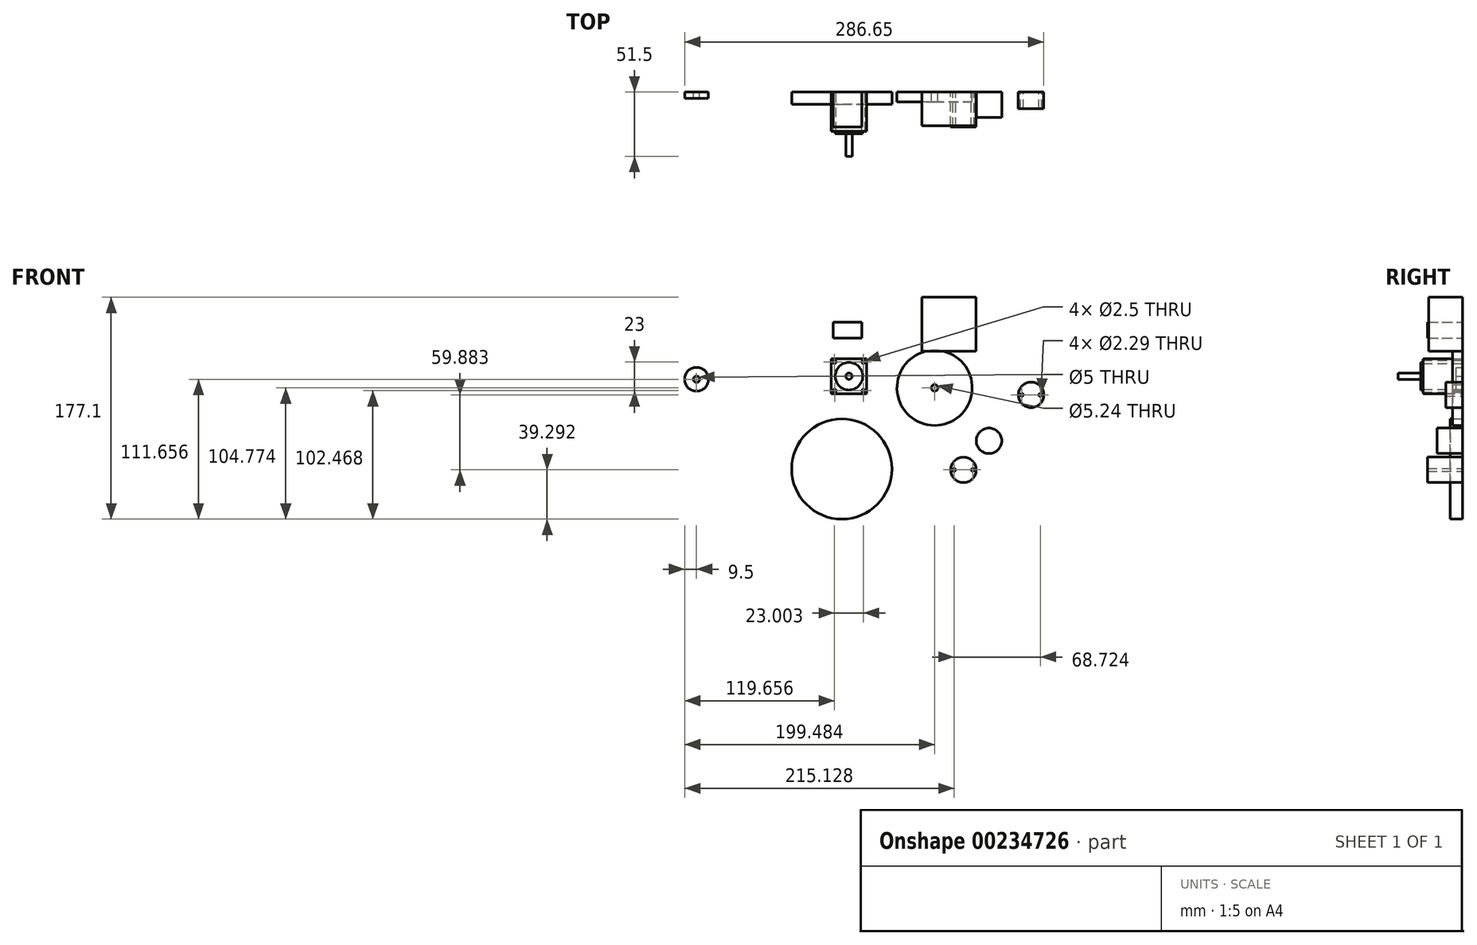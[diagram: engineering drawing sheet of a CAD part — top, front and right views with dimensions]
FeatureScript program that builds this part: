
annotation { "Feature Type Name" : "Feature", "Feature Type Description" : "" }
export const myFeature = defineFeature(function(context is Context, id is Id, definition is map)
    precondition{}
    {
        {
            var Q0;
            Q0=qCreatedBy(makeId("Front.planeOp"),FACE);
            var sketch = newSketch(context, id + "F0", { "sketchPlane" : qUnion([Q0])});
            skLineSegment(sketch, "E0.bottom", {"start": v(-36.47, 8.93) * mm, "end": v(-64.67, 8.93) * mm});
            skLineSegment(sketch, "E0.top", {"start": v(-36.47, 37.13) * mm, "end": v(-64.67, 37.13) * mm});
            skLineSegment(sketch, "E0.left", {"start": v(-36.47, 8.93) * mm, "end": v(-36.47, 37.13) * mm});
            skLineSegment(sketch, "E0.right", {"start": v(-64.67, 8.93) * mm, "end": v(-64.67, 37.13) * mm});
            skPoint(sketch, "E0.middle", {"position": v(-50.57, 23.03) * mm});
            skCircle(sketch, "E1", {"center": v(-50.57, 23.03) * mm, "radius": 2.5 * mm});
            skLineSegment(sketch, "E2", {"start": v(-62.07, 34.43) * mm, "end": v(-39.07, 34.43) * mm});
            skLineSegment(sketch, "E3", {"start": v(-62.07, 11.43) * mm, "end": v(-39.07, 11.43) * mm});
            skCircle(sketch, "E4", {"center": v(-62.07, 34.43) * mm, "radius": 1.25 * mm});
            skCircle(sketch, "E5", {"center": v(-62.07, 11.43) * mm, "radius": 1.25 * mm});
            skCircle(sketch, "E6", {"center": v(-39.07, 11.43) * mm, "radius": 1.25 * mm});
            skCircle(sketch, "E7", {"center": v(-39.07, 34.43) * mm, "radius": 1.25 * mm});
            skCircle(sketch, "E8", {"center": v(-50.57, 23.03) * mm, "radius": 11 * mm});
            skSolve(sketch);
        }
        {
            var Q0;
            Q0=makeQuery(id+"F0.imprint","IMPRINT",FACE,{"disambiguationData":[TD([[makeQuery(id+"F0.imprint","IMPRINT",EDGE,{"derivedFrom":sQuery(id+"F0.wireOp",EDGE,"E1")}),1.0]])]});
            extrude(context, id + "F1", {"entities" : qUnion([Q0]), "depth" : 51.5 * mm});
        }
        {
            var Q0;
            Q0=makeQuery(id+"F0.imprint","IMPRINT",FACE,{"disambiguationData":[TD([[makeQuery(id+"F0.imprint","IMPRINT",EDGE,{"derivedFrom":sQuery(id+"F0.wireOp",EDGE,"E1")}),-1.0]])]});
            extrude(context, id + "F2", {"entities" : qUnion([Q0]), "operationType" : NewBodyOperationType.ADD, "depth" : 33.5 * mm});
        }
        {
            var Q0;
            Q0 = qSketchRegion(id + "F0", true);
            extrude(context, id + "F3", {"entities" : qUnion([Q0]), "operationType" : NewBodyOperationType.ADD, "depth" : 31.5 * mm});
        }
        {
            var Q0;
            Q0=qCreatedBy(makeId("Front.planeOp"),FACE);
            var sketch = newSketch(context, id + "F4", { "sketchPlane" : qUnion([Q0])});
            skCircle(sketch, "E9", {"center": v(17.75, 13.73) * mm, "radius": 30 * mm});
            skCircle(sketch, "E10", {"center": v(17.75, 13.73) * mm, "radius": 2.62 * mm});
            skSolve(sketch);
        }
        {
            var Q0;
            Q0=makeQuery(id+"F4.imprint","IMPRINT",FACE,{"disambiguationData":[TD([[makeQuery(id+"F4.imprint","IMPRINT",EDGE,{"derivedFrom":sQuery(id+"F4.wireOp",EDGE,"E9")}),1.0]])]});
            extrude(context, id + "F5", {"entities" : qUnion([Q0]), "depth" : 8 * mm});
        }
        {
            var Q0;
            Q0=qCreatedBy(makeId("Front.planeOp"),FACE);
            var sketch = newSketch(context, id + "F6", { "sketchPlane" : qUnion([Q0])});
            skCircle(sketch, "E11", {"center": v(-56.28, -51.04) * mm, "radius": 40 * mm});
            skCircle(sketch, "E12", {"center": v(-172.23, 20.62) * mm, "radius": 9.5 * mm});
            skCircle(sketch, "E13", {"center": v(-172.23, 20.62) * mm, "radius": 2.5 * mm});
            skSolve(sketch);
        }
        {
            var Q0;
            Q0=makeQuery(id+"F6.imprint","IMPRINT",FACE,{"disambiguationData":[TD([[makeQuery(id+"F6.imprint","IMPRINT",EDGE,{"derivedFrom":sQuery(id+"F6.wireOp",EDGE,"E11")}),1.0]])]});
            extrude(context, id + "F7", {"entities" : qUnion([Q0]), "depth" : 10 * mm});
        }
        {
            var Q0;
            Q0=qCreatedBy(makeId("Front.planeOp"),FACE);
            var sketch = newSketch(context, id + "F8", { "sketchPlane" : qUnion([Q0])});
            skCircle(sketch, "E14", {"center": v(40.76, -51.75) * mm, "radius": 10.16 * mm});
            skCircle(sketch, "E15", {"center": v(61.22, -28.51) * mm, "radius": 10.16 * mm});
            skLineSegment(sketch, "E16", {"start": v(51.06, -28.51) * mm, "end": v(71.38, -28.51) * mm});
            skCircle(sketch, "E17", {"center": v(33.4, -51.75) * mm, "radius": 1.14 * mm});
            skCircle(sketch, "E18", {"center": v(48.13, -51.75) * mm, "radius": 1.14 * mm});
            skLineSegment(sketch, "E19", {"start": v(33.4, -51.75) * mm, "end": v(30.6, -51.75) * mm});
            skLineSegment(sketch, "E20", {"start": v(48.13, -51.75) * mm, "end": v(50.92, -51.75) * mm});
            skCircle(sketch, "E21", {"center": v(94.76, 8.14) * mm, "radius": 10.16 * mm});
            skLineSegment(sketch, "E22", {"start": v(94.76, 8.14) * mm, "end": v(102.12, 8.14) * mm});
            skLineSegment(sketch, "E23", {"start": v(94.76, 8.14) * mm, "end": v(87.39, 8.14) * mm});
            skCircle(sketch, "E24", {"center": v(87.39, 8.14) * mm, "radius": 1.14 * mm});
            skCircle(sketch, "E25", {"center": v(102.12, 8.14) * mm, "radius": 1.14 * mm});
            skSolve(sketch);
        }
        {
            var Q0;
            Q0=makeQuery(id+"F8.imprint","IMPRINT",FACE,{"disambiguationData":[TD([[makeQuery(id+"F8.imprint","IMPRINT",EDGE,{"derivedFrom":sQuery(id+"F8.wireOp",EDGE,"E14")}),1.0]])]});
            extrude(context, id + "F9", {"entities" : qUnion([Q0]), "depth" : 27.94 * mm});
        }
        {
            var Q0;
            Q0=makeQuery(id+"F8.imprint","IMPRINT",FACE,{"disambiguationData":[TD([[makeQuery(id+"F8.imprint","IMPRINT",EDGE,{"derivedFrom":sQuery(id+"F8.wireOp",EDGE,"E15")}),1.0]])]});
            extrude(context, id + "F10", {"entities" : qUnion([Q0]), "depth" : 20.32 * mm});
        }
        {
            var Q0;
            Q0=qCreatedBy(makeId("Front.planeOp"),FACE);
            var sketch = newSketch(context, id + "F11", { "sketchPlane" : qUnion([Q0])});
            skLineSegment(sketch, "E26.bottom", {"start": v(139.7, -107.95) * mm, "end": v(-139.7, -107.95) * mm});
            skLineSegment(sketch, "E26.top", {"start": v(139.7, 107.95) * mm, "end": v(-139.7, 107.95) * mm});
            skLineSegment(sketch, "E26.left", {"start": v(139.7, -107.95) * mm, "end": v(139.7, 107.95) * mm});
            skLineSegment(sketch, "E26.right", {"start": v(-139.7, -107.95) * mm, "end": v(-139.7, 107.95) * mm});
            skPoint(sketch, "E26.middle", {"position": v(0, 0) * mm});
            skSolve(sketch);
        }
        {
            var Q0;
            Q0=qCreatedBy(makeId("Front.planeOp"),FACE);
            var sketch = newSketch(context, id + "F12", { "sketchPlane" : qUnion([Q0])});
            skLineSegment(sketch, "E27.bottom", {"start": v(50.67, 42.88) * mm, "end": v(7.49, 42.88) * mm});
            skLineSegment(sketch, "E27.top", {"start": v(50.67, 86.06) * mm, "end": v(7.49, 86.06) * mm});
            skLineSegment(sketch, "E27.left", {"start": v(50.67, 42.88) * mm, "end": v(50.67, 86.06) * mm});
            skLineSegment(sketch, "E27.right", {"start": v(7.49, 42.88) * mm, "end": v(7.49, 86.06) * mm});
            skPoint(sketch, "E27.middle", {"position": v(29.08, 64.47) * mm});
            skSolve(sketch);
        }
        {
            var Q0;
            Q0 = qSketchRegion(id + "F12", true);
            extrude(context, id + "F13", {"entities" : qUnion([Q0]), "depth" : 27 * mm});
        }
        {
            var Q0;
            Q0=qCreatedBy(makeId("Front.planeOp"),FACE);
            var sketch = newSketch(context, id + "F14", { "sketchPlane" : qUnion([Q0])});
            skLineSegment(sketch, "E28.bottom", {"start": v(-63.04, 66.06) * mm, "end": v(-40.18, 66.06) * mm});
            skLineSegment(sketch, "E28.top", {"start": v(-63.04, 53.36) * mm, "end": v(-40.18, 53.36) * mm});
            skLineSegment(sketch, "E28.left", {"start": v(-63.04, 66.06) * mm, "end": v(-63.04, 53.36) * mm});
            skLineSegment(sketch, "E28.right", {"start": v(-40.18, 66.06) * mm, "end": v(-40.18, 53.36) * mm});
            skCircle(sketch, "E29", {"center": v(9.1, -33.26) * mm, "radius": 10.16 * mm});
            skLineSegment(sketch, "E30", {"start": v(9.1, -33.26) * mm, "end": v(16.46, -33.26) * mm});
            skLineSegment(sketch, "E31", {"start": v(9.1, -33.26) * mm, "end": v(1.73, -33.26) * mm});
            skCircle(sketch, "E32", {"center": v(1.73, -33.26) * mm, "radius": 1.14 * mm});
            skCircle(sketch, "E33", {"center": v(16.46, -33.26) * mm, "radius": 1.14 * mm});
            skSolve(sketch);
        }
        {
            var Q0;
            Q0=makeQuery(id+"F14.imprint","IMPRINT",FACE,{"disambiguationData":[TD([[makeQuery(id+"F14.imprint","IMPRINT",EDGE,{"derivedFrom":sQuery(id+"F14.wireOp",EDGE,"E28.bottom")}),-1.0]])]});
            extrude(context, id + "F15", {"entities" : qUnion([Q0]), "depth" : 27.94 * mm});
        }
        {
            var Q0;
            Q0=makeQuery(id+"F8.imprint","IMPRINT",FACE,{"disambiguationData":[TD([[makeQuery(id+"F8.imprint","IMPRINT",EDGE,{"derivedFrom":sQuery(id+"F8.wireOp",EDGE,"E21")}),1.0]])]});
            extrude(context, id + "F16", {"entities" : qUnion([Q0]), "depth" : 13.46 * mm});
        }
        {
            var Q0;
            Q0=makeQuery(id+"F6.imprint","IMPRINT",FACE,{"disambiguationData":[TD([[makeQuery(id+"F6.imprint","IMPRINT",EDGE,{"derivedFrom":sQuery(id+"F6.wireOp",EDGE,"E12")}),1.0]])]});
            extrude(context, id + "F17", {"entities" : qUnion([Q0]), "operationType" : NewBodyOperationType.ADD, "depth" : 5 * mm});
        }
    });
